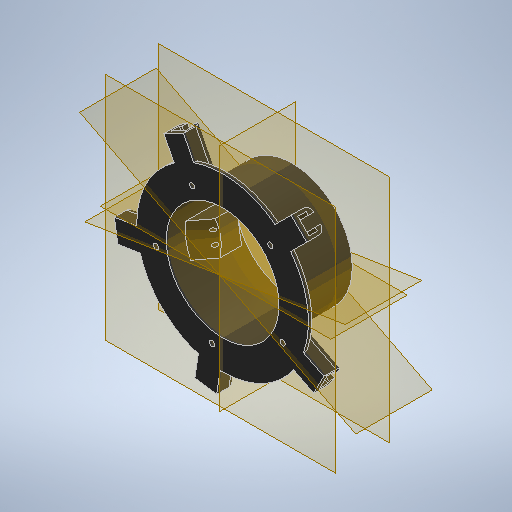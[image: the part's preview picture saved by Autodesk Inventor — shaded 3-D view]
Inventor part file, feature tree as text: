
AUTODESK INVENTOR PART (.ipt)
format: ipt  version: 2025.1 (Build 291241020, 241B)  size: 500,736 bytes
history: native  units: mm
features: extrude x8, sketch x8, plane x4, fillet x3, mirror x2, pattern_circular x1, revolve x1, chamfer x1, projected_geometry x1
ambient origin geometry x8: Origin, YZ Plane, XZ Plane, XY Plane, X Axis, Y Axis, Z Axis, Center Point
bodies: Body1 (feature_tree)
feature tree (29):
  extrude  "Extrusion6"  Depth=92.0mm
  extrude  "Extrusion8"  TaperAngle=45.0deg  [1 undecoded]
  sketch  "Sketch9"  dims[d30=2.75mm d31=0.0mm d32=45.0deg]
  extrude  "Extrusion7"  Depth=18.0mm
  extrude  "Extrusion9"  Depth=50.0mm TaperAngle=360.0deg
  plane  "Work Plane1"
  mirror  "Mirror1"
  extrude  "Extrusion11"  Depth=56.75mm TaperAngle=0.0deg
  extrude  "Extrusion10"  Depth=5.0mm
  fillet  "Fillet5"  Radius=4.5mm
  pattern_circular  "Circular Pattern1"  [2 undecoded]
  plane  "Work Plane2"
  plane  "Work Plane3"
  plane  "Work Plane4"
  extrude  "Extrusion12"  Depth=10.0mm
  revolve  "Revolution1"  [1 undecoded]
  extrude  "Extrusion14"  Depth=10.0mm TaperAngle=0.0deg
  mirror  "Mirror2"
  fillet  "Fillet6"  Radius=5.0mm
  chamfer  "Chamfer1"  [1 undecoded]
  fillet  "Fillet7"  Radius=26.0mm
  sketch  "Sketch8"  dims[d28=140.0mm d29=92.0mm]
  sketch  "Sketch10"  dims[d33=88.0mm d34=18.0mm]
  sketch  "Sketch11"  dims[d36=3.75mm d37=0.0mm d38=50.0mm d39=360.0deg]
  sketch  "Sketch12"  dims[d41=98.0mm d42=56.75mm d43=0.0mm]
  projected_geometry  "Projected Loop1"
  sketch  "Sketch13"  dims[d44=15.0mm d45=5.0mm d46=4.5mm]
  sketch  "Sketch14"  dims[d47=2.5mm]
  sketch  "Sketch15"  dims[d49=56.75mm d50=0.0mm d51=55.0mm d52=4.3mm d53=0.0mm d54=0.0mm d55=0.05mm d56=0.0mm d58=5.0mm d59=-44.75mm d60=26.0mm d61=31.75mm d62=29.25mm d63=0.0mm d64=15.0mm d67=3.0mm d68=10.0mm d69=2.5mm d72=13.0mm d75=6.0mm d77=5.0mm d78=11.25mm d79=8.0mm d80=2.5mm d81=3.0mm d82=14.0mm d83=0.0mm d84=7.0mm d85=15.0mm d86=2.0mm d87=45.0deg d88=10.0mm d89=45.0deg]
note: 5 required parameter values undecoded (feature->parameter linkage not recoverable at this tier; creation-order binding heuristic only, values carry confidence <= 0.55)